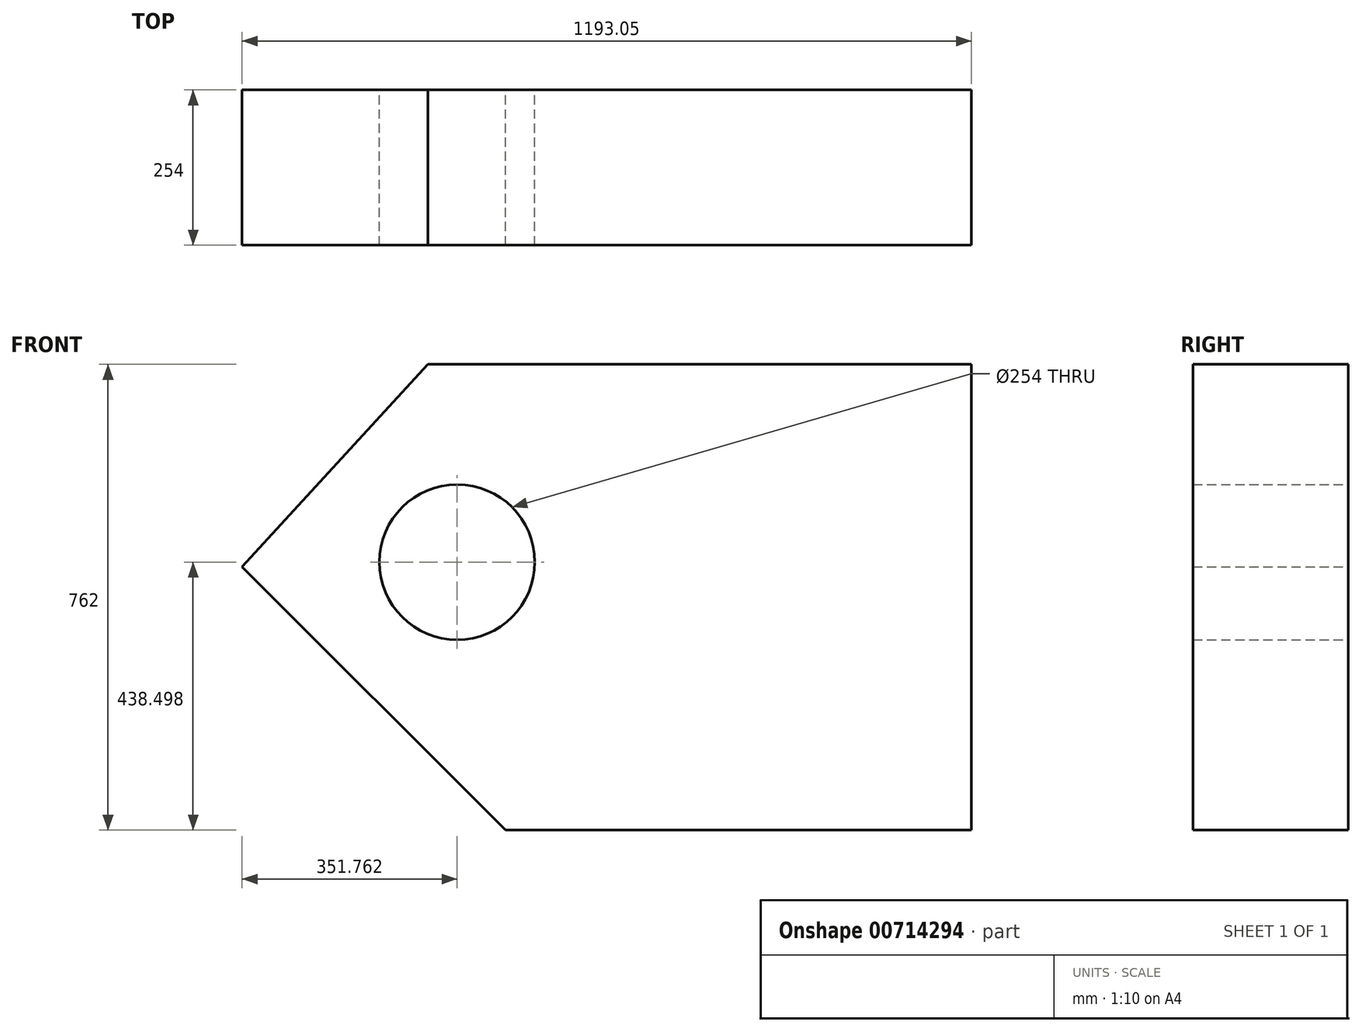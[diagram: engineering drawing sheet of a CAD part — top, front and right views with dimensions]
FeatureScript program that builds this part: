
annotation { "Feature Type Name" : "Feature", "Feature Type Description" : "" }
export const myFeature = defineFeature(function(context is Context, id is Id, definition is map)
    precondition{}
    {
        {
            var Q0;
            Q0=qCreatedBy(makeId("Front.planeOp"),FACE);
            var sketch = newSketch(context, id + "F0", { "sketchPlane" : qUnion([Q0])});
            skLineSegment(sketch, "E0", {"start": v(0, 0) * mm, "end": v(762, 0) * mm});
            skLineSegment(sketch, "E1", {"start": v(762, 0) * mm, "end": v(762, 762) * mm});
            skLineSegment(sketch, "E2", {"start": v(762, 762) * mm, "end": v(-127, 762) * mm});
            skLineSegment(sketch, "E3", {"start": v(0, 0) * mm, "end": v(-431.05, 431.05) * mm});
            skLineSegment(sketch, "E4", {"start": v(-127, 762) * mm, "end": v(-431.05, 431.05) * mm});
            skCircle(sketch, "E5", {"center": v(-79.29, 438.5) * mm, "radius": 127 * mm});
            skSolve(sketch);
        }
        {
            var Q0;
            Q0 = qSketchRegion(id + "F0", true);
            extrude(context, id + "F1", {"entities" : qUnion([Q0]), "depth" : 254 * mm, "offsetDistance" : 25.4 * mm});
        }
    });
